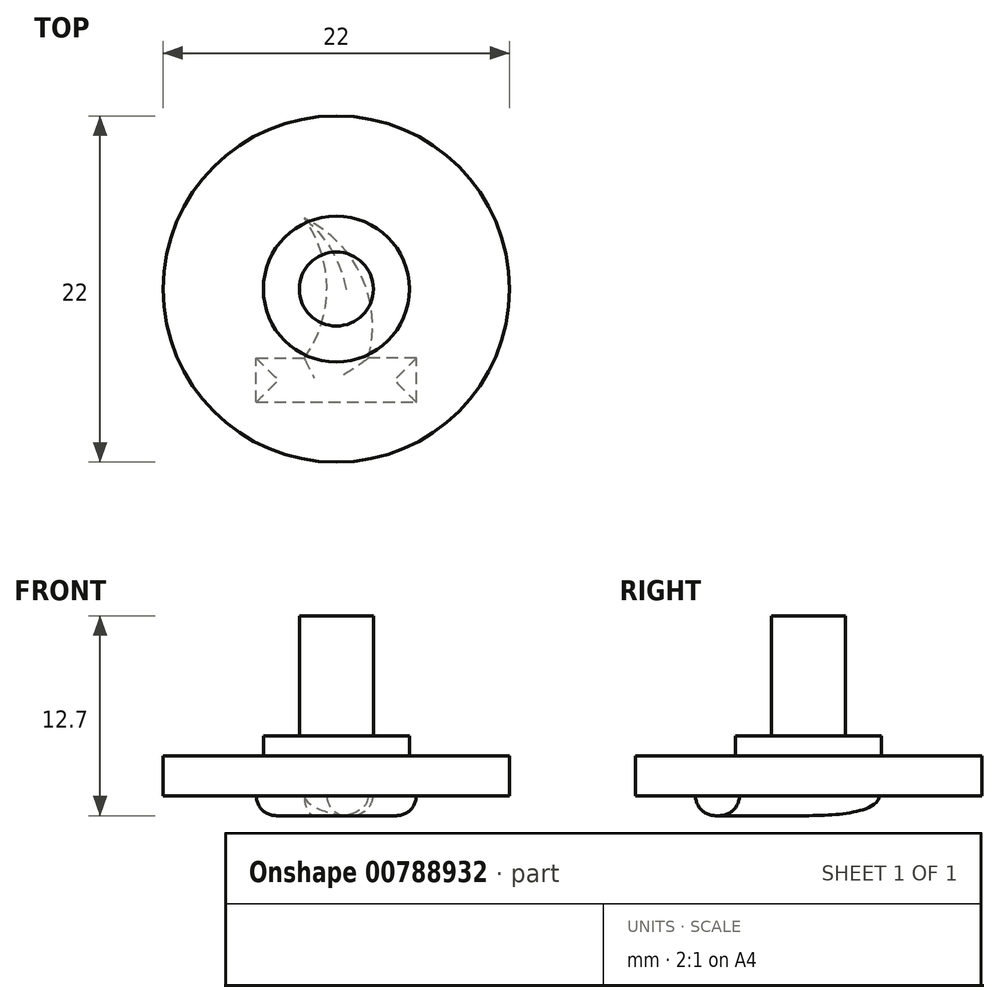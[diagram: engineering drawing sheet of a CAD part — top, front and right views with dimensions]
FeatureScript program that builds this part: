
annotation { "Feature Type Name" : "Feature", "Feature Type Description" : "" }
export const myFeature = defineFeature(function(context is Context, id is Id, definition is map)
    precondition{}
    {
        {
            var Q0;
            Q0=qCreatedBy(makeId("Top.planeOp"),FACE);
            var sketch = newSketch(context, id + "F0", { "sketchPlane" : qUnion([Q0])});
            skCircle(sketch, "E0", {"center": v(0, 0) * mm, "radius": 11 * mm});
            skCircle(sketch, "E1", {"center": v(0, 0) * mm, "radius": 4.64 * mm});
            skCircle(sketch, "E2", {"center": v(0, 0) * mm, "radius": 2.35 * mm});
            skSolve(sketch);
        }
        {
            var Q0;
            Q0=makeQuery(id+"F0.imprint","IMPRINT",FACE,{"disambiguationData":[TD([[makeQuery(id+"F0.imprint","IMPRINT",EDGE,{"derivedFrom":sQuery(id+"F0.wireOp",EDGE,"E2")}),1.0]])]});
            extrude(context, id + "F1", {"entities" : qUnion([Q0]), "depth" : 11.43 * mm, "offsetDistance" : 25.4 * mm});
        }
        {
            var Q0;
            Q0=makeQuery(id+"F0.imprint","IMPRINT",FACE,{"disambiguationData":[TD([[makeQuery(id+"F0.imprint","IMPRINT",EDGE,{"derivedFrom":sQuery(id+"F0.wireOp",EDGE,"E1")}),1.0]])]});
            extrude(context, id + "F2", {"entities" : qUnion([Q0]), "operationType" : NewBodyOperationType.ADD, "depth" : 3.8 * mm, "offsetDistance" : 25.4 * mm});
        }
        {
            var Q0;
            Q0=makeQuery(id+"F0.imprint","IMPRINT",FACE,{"disambiguationData":[TD([[makeQuery(id+"F0.imprint","IMPRINT",EDGE,{"derivedFrom":sQuery(id+"F0.wireOp",EDGE,"E0")}),1.0]])]});
            extrude(context, id + "F3", {"entities" : qUnion([Q0]), "operationType" : NewBodyOperationType.ADD, "depth" : 2.54 * mm, "offsetDistance" : 25.4 * mm});
        }
        {
            var Q0;
            Q0=makeQuery(id+"F0.imprint","IMPRINT",FACE,{"disambiguationData":[TD([[makeQuery(id+"F0.imprint","IMPRINT",EDGE,{"derivedFrom":sQuery(id+"F0.wireOp",EDGE,"E0")}),1.0]])]});
            var sketch = newSketch(context, id + "F4", { "sketchPlane" : qUnion([Q0])});
            skLineSegment(sketch, "E3", {"start": v(-5.08, -7.19) * mm, "end": v(5.08, -7.19) * mm});
            skLineSegment(sketch, "E4", {"start": v(5.08, -7.19) * mm, "end": v(5.08, -4.4) * mm});
            skLineSegment(sketch, "E5", {"start": v(5.08, -4.4) * mm, "end": v(2.03, -4.4) * mm});
            skLineSegment(sketch, "E6", {"start": v(-5.08, -7.19) * mm, "end": v(-5.08, -4.4) * mm});
            skLineSegment(sketch, "E7", {"start": v(-5.08, -4.4) * mm, "end": v(-2.03, -4.4) * mm});
            skArc(sketch, "E8", {"start": v(2.03, -4.4) * mm, "mid": v(1.61, 0.79) * mm, "end": v(-2.03, 4.5) * mm});
            skArc(sketch, "E9", {"start": v(-2.03, -4.4) * mm, "mid": v(-0.6, 0.05) * mm, "end": v(-2.03, 4.5) * mm});
            skSolve(sketch);
        }
        {
            var Q0;
            Q0 = qSketchRegion(id + "F4", true);
            extrude(context, id + "F5", {"entities" : qUnion([Q0]), "operationType" : NewBodyOperationType.ADD, "oppositeDirection" : true, "depth" : 1.27 * mm, "offsetDistance" : 25.4 * mm});
        }
        {
            var Q0;
            Q0=makeQuery(id+"F5.opExtrude","CAP_EDGE",EDGE,{"disambiguationData":[OSD([sQuery(id+"F4.wireOp",EDGE,"E4")])],"isStart":false});
            var Q1;
            Q1=makeQuery(id+"F5.opExtrude","CAP_EDGE",EDGE,{"disambiguationData":[OSD([sQuery(id+"F4.wireOp",EDGE,"E6")])],"isStart":false});
            var Q2;
            Q2=makeQuery(id+"F5.opExtrude","CAP_EDGE",EDGE,{"disambiguationData":[OSD([sQuery(id+"F4.wireOp",EDGE,"E3")])],"isStart":false});
            var Q3;
            Q3=makeQuery(id+"F5.opExtrude","CAP_EDGE",EDGE,{"disambiguationData":[OSD([sQuery(id+"F4.wireOp",EDGE,"E7")])],"isStart":false});
            var Q4;
            Q4=makeQuery(id+"F5.opExtrude","CAP_EDGE",EDGE,{"disambiguationData":[OSD([sQuery(id+"F4.wireOp",EDGE,"E5")])],"isStart":false});
            var Q5;
            Q5=makeQuery(id+"F5.opExtrude","CAP_EDGE",EDGE,{"disambiguationData":[OSD([sQuery(id+"F4.wireOp",EDGE,"E8")])],"isStart":false});
            var Q6;
            Q6=makeQuery(id+"F5.opExtrude","CAP_EDGE",EDGE,{"disambiguationData":[OSD([sQuery(id+"F4.wireOp",EDGE,"E9")])],"isStart":false});
            fillet(context, id + "F6", {"entities" : qUnion([Q0, Q1, Q2, Q3, Q4, Q5, Q6]), "radius" : 1.27 * mm, "tangentPropagation" : true, "allowEdgeOverflow" : false});
        }
    });
